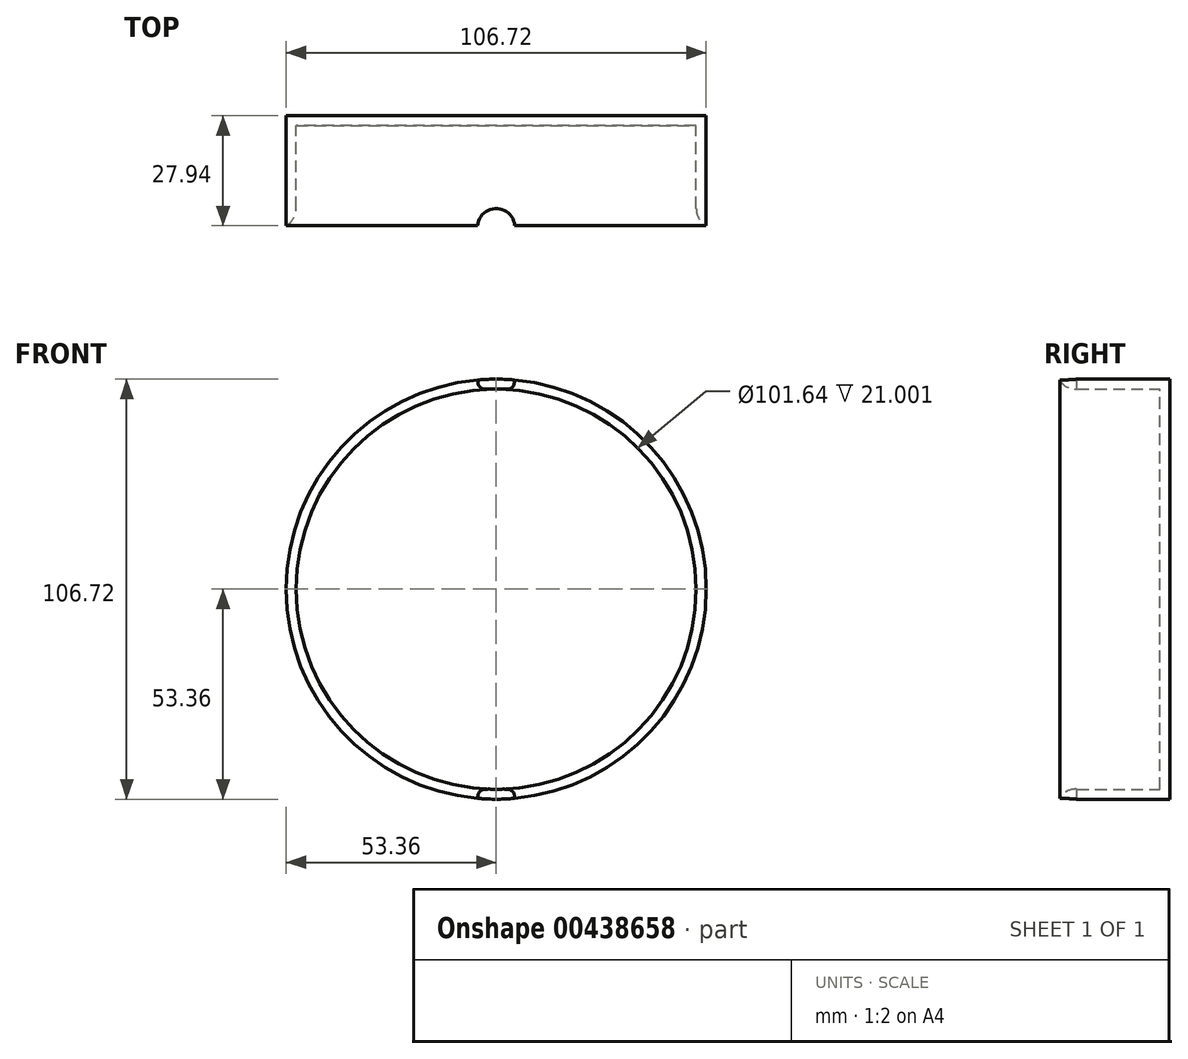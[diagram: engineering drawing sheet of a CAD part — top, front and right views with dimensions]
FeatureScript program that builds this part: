
annotation { "Feature Type Name" : "Feature", "Feature Type Description" : "" }
export const myFeature = defineFeature(function(context is Context, id is Id, definition is map)
    precondition{}
    {
        {
            var Q0;
            Q0=qCreatedBy(makeId("Front.planeOp"),FACE);
            var sketch = newSketch(context, id + "F0", { "sketchPlane" : qUnion([Q0])});
            skCircle(sketch, "E0", {"center": v(0, 0) * mm, "radius": 53.36 * mm});
            skSolve(sketch);
        }
        {
            var Q0;
            Q0=makeQuery(id+"F0.imprint","IMPRINT",FACE,{"disambiguationData":[TD([[makeQuery(id+"F0.imprint","IMPRINT",EDGE,{"derivedFrom":sQuery(id+"F0.wireOp",EDGE,"E0")}),1.0]])]});
            extrude(context, id + "F1", {"entities" : qUnion([Q0]), "depth" : 2.54 * mm});
        }
        {
            var Q0;
            Q0=makeQuery(id+"F1.opExtrude","CAP_FACE",FACE,{"disambiguationData":[OSD([sQuery(id+"F0.wireOp",EDGE,"E0")])],"isStart":false});
            var sketch = newSketch(context, id + "F2", { "sketchPlane" : qUnion([Q0])});
            skCircle(sketch, "E1.0", {"center": v(0, 0) * mm, "radius": 50.82 * mm});
            skCircle(sketch, "E2.0", {"center": v(0, 0) * mm, "radius": 53.36 * mm});
            skSolve(sketch);
        }
        {
            var Q0;
            Q0=makeQuery(id+"F2.imprint","IMPRINT",FACE,{"disambiguationData":[TD([[makeQuery(id+"F2.imprint","IMPRINT",EDGE,{"derivedFrom":sQuery(id+"F2.wireOp",EDGE,"E1.0")}),-1.0]])]});
            extrude(context, id + "F3", {"entities" : qUnion([Q0]), "operationType" : NewBodyOperationType.ADD, "depth" : 25.4 * mm});
        }
        {
            var Q0;
            Q0=makeQuery(id+"F3.opExtrude","CAP_EDGE",EDGE,{"disambiguationData":[OSD([sQuery(id+"F2.wireOp",EDGE,"E1.0")])],"isStart":false});
            fillet(context, id + "F4", {"entities" : qUnion([Q0]), "radius" : 5.08 * mm, "tangentPropagation" : true, "allowEdgeOverflow" : false});
        }
        {
            var Q0;
            Q0=qCreatedBy(makeId("Top.planeOp"),FACE);
            var sketch = newSketch(context, id + "F5", { "sketchPlane" : qUnion([Q0])});
            skCircle(sketch, "E3", {"center": v(0, -28.3) * mm, "radius": 4.73 * mm});
            skSolve(sketch);
        }
        {
            var Q0;
            Q0=makeQuery(id+"F5.imprint","IMPRINT",FACE,{"disambiguationData":[TD([[makeQuery(id+"F5.imprint","IMPRINT",EDGE,{"derivedFrom":sQuery(id+"F5.wireOp",EDGE,"E3")}),1.0]])]});
            extrude(context, id + "F6", {"entities" : qUnion([Q0]), "operationType" : NewBodyOperationType.REMOVE, "endBound" : BoundingType.THROUGH_ALL, "oppositeDirection" : true, "depth" : 25.4 * mm, "hasSecondDirection" : true, "secondDirectionBound" : SecondDirectionBoundingType.THROUGH_ALL, "secondDirectionOppositeDirection" : false, "secondDirectionDepth" : 25.4 * mm});
        }
    });
